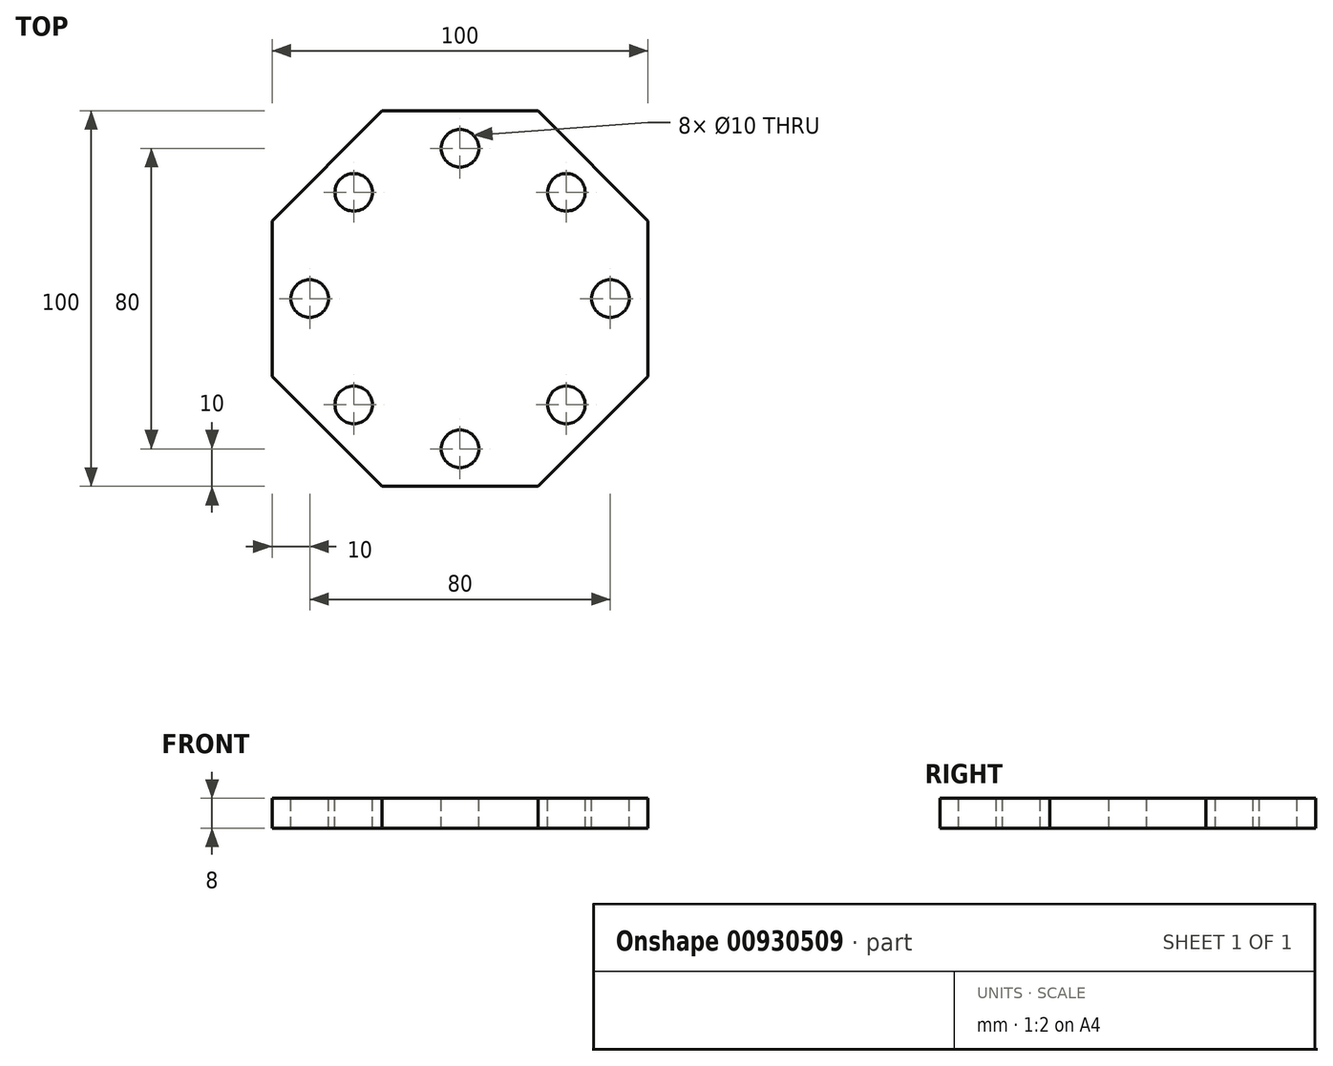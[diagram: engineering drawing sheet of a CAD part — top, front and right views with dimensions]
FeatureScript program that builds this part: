
annotation { "Feature Type Name" : "Feature", "Feature Type Description" : "" }
export const myFeature = defineFeature(function(context is Context, id is Id, definition is map)
    precondition{}
    {
        {
            var Q0;
            Q0=qCreatedBy(makeId("Top.planeOp"),FACE);
            var sketch = newSketch(context, id + "F0", { "sketchPlane" : qUnion([Q0])});
            skCircle(sketch, "E0.cCircle", {"center": v(0, 0) * mm, "radius": 50 * mm, "construction": true});
            skLineSegment(sketch, "E0.0", {"start": v(50, -20.71) * mm, "end": v(20.71, -50) * mm});
            skLineSegment(sketch, "E0.1", {"start": v(20.71, -50) * mm, "end": v(-20.71, -50) * mm});
            skLineSegment(sketch, "E0.2", {"start": v(-20.71, -50) * mm, "end": v(-50, -20.71) * mm});
            skLineSegment(sketch, "E0.3", {"start": v(-50, -20.71) * mm, "end": v(-50, 20.71) * mm});
            skLineSegment(sketch, "E0.4", {"start": v(-50, 20.71) * mm, "end": v(-20.71, 50) * mm});
            skLineSegment(sketch, "E0.5", {"start": v(-20.71, 50) * mm, "end": v(20.71, 50) * mm});
            skLineSegment(sketch, "E0.6", {"start": v(20.71, 50) * mm, "end": v(50, 20.71) * mm});
            skLineSegment(sketch, "E0.7", {"start": v(50, 20.71) * mm, "end": v(50, -20.71) * mm});
            skPoint(sketch, "E0.0.midPoint", {"position": v(35.36, -35.36) * mm});
            skSolve(sketch);
        }
        {
            var Q0;
            Q0 = qSketchRegion(id + "F0", true);
            extrude(context, id + "F1", {"entities" : qUnion([Q0]), "depth" : 8 * mm, "offsetDistance" : 25 * mm});
        }
        {
            var Q0;
            Q0=makeQuery(id+"F1.opExtrude","CAP_FACE",FACE,{"disambiguationData":[OSD([sQuery(id+"F0.wireOp",EDGE,"E0.0"),sQuery(id+"F0.wireOp",EDGE,"E0.1"),sQuery(id+"F0.wireOp",EDGE,"E0.2"),sQuery(id+"F0.wireOp",EDGE,"E0.3"),sQuery(id+"F0.wireOp",EDGE,"E0.4"),sQuery(id+"F0.wireOp",EDGE,"E0.5"),sQuery(id+"F0.wireOp",EDGE,"E0.6"),sQuery(id+"F0.wireOp",EDGE,"E0.7")])],"isStart":false});
            var sketch = newSketch(context, id + "F2", { "sketchPlane" : qUnion([Q0])});
            skCircle(sketch, "E1", {"center": v(0, 0) * mm, "radius": 40 * mm});
            skCircle(sketch, "E2", {"center": v(0, 40) * mm, "radius": 5 * mm});
            skCircle(sketch, "E3", {"center": v(0, -40) * mm, "radius": 5 * mm});
            skCircle(sketch, "E4", {"center": v(40, 0) * mm, "radius": 5 * mm});
            skCircle(sketch, "E5", {"center": v(-40, 0) * mm, "radius": 5 * mm});
            skCircle(sketch, "E6", {"center": v(-28.28, 28.28) * mm, "radius": 5 * mm});
            skCircle(sketch, "E7", {"center": v(28.28, 28.28) * mm, "radius": 5 * mm});
            skCircle(sketch, "E8", {"center": v(28.28, -28.28) * mm, "radius": 5 * mm});
            skCircle(sketch, "E9", {"center": v(-28.28, -28.28) * mm, "radius": 5 * mm});
            skSolve(sketch);
        }
        {
            var Q0;
            {var subQ0=sQuery(id+"F2.wireOp",EDGE,"E7");var subQ1=sQuery(id+"F2.wireOp",EDGE,"E1");var subQ2=makeQuery(id+"F2.imprint","INTERSECT",VERTEX,{"disambiguationData":[OD(0.0)],"derivedFrom":[subQ1,subQ0]});Q0=makeQuery(id+"F2.imprint","IMPRINT",FACE,{"disambiguationData":[TD([[makeQuery(id+"F2.imprint","IMPRINT",EDGE,{"disambiguationData":[TD([[subQ2,-1.0]])],"derivedFrom":subQ1}),1.0]])]});}
            var Q1;
            {var subQ0=sQuery(id+"F2.wireOp",EDGE,"E7");var subQ1=sQuery(id+"F2.wireOp",EDGE,"E1");var subQ2=makeQuery(id+"F2.imprint","INTERSECT",VERTEX,{"disambiguationData":[OD(0.0)],"derivedFrom":[subQ1,subQ0]});Q1=makeQuery(id+"F2.imprint","IMPRINT",FACE,{"disambiguationData":[TD([[makeQuery(id+"F2.imprint","IMPRINT",EDGE,{"disambiguationData":[TD([[subQ2,-1.0]])],"derivedFrom":subQ1}),-1.0]])]});}
            var Q2;
            {var subQ0=sQuery(id+"F2.wireOp",EDGE,"E2");var subQ1=sQuery(id+"F2.wireOp",EDGE,"E1");var subQ2=makeQuery(id+"F2.imprint","INTERSECT",VERTEX,{"disambiguationData":[OD(0.0)],"derivedFrom":[subQ1,subQ0]});Q2=makeQuery(id+"F2.imprint","IMPRINT",FACE,{"disambiguationData":[TD([[makeQuery(id+"F2.imprint","IMPRINT",EDGE,{"disambiguationData":[TD([[subQ2,-1.0]])],"derivedFrom":subQ1}),1.0]])]});}
            var Q3;
            {var subQ0=sQuery(id+"F2.wireOp",EDGE,"E2");var subQ1=sQuery(id+"F2.wireOp",EDGE,"E1");var subQ2=makeQuery(id+"F2.imprint","INTERSECT",VERTEX,{"disambiguationData":[OD(0.0)],"derivedFrom":[subQ1,subQ0]});Q3=makeQuery(id+"F2.imprint","IMPRINT",FACE,{"disambiguationData":[TD([[makeQuery(id+"F2.imprint","IMPRINT",EDGE,{"disambiguationData":[TD([[subQ2,-1.0]])],"derivedFrom":subQ1}),-1.0]])]});}
            var Q4;
            {var subQ0=sQuery(id+"F2.wireOp",EDGE,"E6");var subQ1=sQuery(id+"F2.wireOp",EDGE,"E1");var subQ2=makeQuery(id+"F2.imprint","INTERSECT",VERTEX,{"disambiguationData":[OD(0.0)],"derivedFrom":[subQ1,subQ0]});Q4=makeQuery(id+"F2.imprint","IMPRINT",FACE,{"disambiguationData":[TD([[makeQuery(id+"F2.imprint","IMPRINT",EDGE,{"disambiguationData":[TD([[subQ2,-1.0]])],"derivedFrom":subQ1}),-1.0]])]});}
            var Q5;
            {var subQ0=sQuery(id+"F2.wireOp",EDGE,"E6");var subQ1=sQuery(id+"F2.wireOp",EDGE,"E1");var subQ2=makeQuery(id+"F2.imprint","INTERSECT",VERTEX,{"disambiguationData":[OD(0.0)],"derivedFrom":[subQ1,subQ0]});Q5=makeQuery(id+"F2.imprint","IMPRINT",FACE,{"disambiguationData":[TD([[makeQuery(id+"F2.imprint","IMPRINT",EDGE,{"disambiguationData":[TD([[subQ2,-1.0]])],"derivedFrom":subQ1}),1.0]])]});}
            var Q6;
            {var subQ0=sQuery(id+"F2.wireOp",EDGE,"E5");var subQ1=sQuery(id+"F2.wireOp",EDGE,"E1");var subQ2=makeQuery(id+"F2.imprint","INTERSECT",VERTEX,{"disambiguationData":[OD(0.0)],"derivedFrom":[subQ1,subQ0]});Q6=makeQuery(id+"F2.imprint","IMPRINT",FACE,{"disambiguationData":[TD([[makeQuery(id+"F2.imprint","IMPRINT",EDGE,{"disambiguationData":[TD([[subQ2,-1.0]])],"derivedFrom":subQ1}),-1.0]])]});}
            var Q7;
            {var subQ0=sQuery(id+"F2.wireOp",EDGE,"E5");var subQ1=sQuery(id+"F2.wireOp",EDGE,"E1");var subQ2=makeQuery(id+"F2.imprint","INTERSECT",VERTEX,{"disambiguationData":[OD(0.0)],"derivedFrom":[subQ1,subQ0]});Q7=makeQuery(id+"F2.imprint","IMPRINT",FACE,{"disambiguationData":[TD([[makeQuery(id+"F2.imprint","IMPRINT",EDGE,{"disambiguationData":[TD([[subQ2,-1.0]])],"derivedFrom":subQ1}),1.0]])]});}
            var Q8;
            {var subQ0=sQuery(id+"F2.wireOp",EDGE,"E9");var subQ1=sQuery(id+"F2.wireOp",EDGE,"E1");var subQ2=makeQuery(id+"F2.imprint","INTERSECT",VERTEX,{"disambiguationData":[OD(0.0)],"derivedFrom":[subQ1,subQ0]});Q8=makeQuery(id+"F2.imprint","IMPRINT",FACE,{"disambiguationData":[TD([[makeQuery(id+"F2.imprint","IMPRINT",EDGE,{"disambiguationData":[TD([[subQ2,-1.0]])],"derivedFrom":subQ1}),-1.0]])]});}
            var Q9;
            {var subQ0=sQuery(id+"F2.wireOp",EDGE,"E9");var subQ1=sQuery(id+"F2.wireOp",EDGE,"E1");var subQ2=makeQuery(id+"F2.imprint","INTERSECT",VERTEX,{"disambiguationData":[OD(0.0)],"derivedFrom":[subQ1,subQ0]});Q9=makeQuery(id+"F2.imprint","IMPRINT",FACE,{"disambiguationData":[TD([[makeQuery(id+"F2.imprint","IMPRINT",EDGE,{"disambiguationData":[TD([[subQ2,-1.0]])],"derivedFrom":subQ1}),1.0]])]});}
            var Q10;
            {var subQ0=sQuery(id+"F2.wireOp",EDGE,"E3");var subQ1=sQuery(id+"F2.wireOp",EDGE,"E1");var subQ2=makeQuery(id+"F2.imprint","INTERSECT",VERTEX,{"disambiguationData":[OD(0.0)],"derivedFrom":[subQ1,subQ0]});Q10=makeQuery(id+"F2.imprint","IMPRINT",FACE,{"disambiguationData":[TD([[makeQuery(id+"F2.imprint","IMPRINT",EDGE,{"disambiguationData":[TD([[subQ2,-1.0]])],"derivedFrom":subQ1}),1.0]])]});}
            var Q11;
            {var subQ0=sQuery(id+"F2.wireOp",EDGE,"E3");var subQ1=sQuery(id+"F2.wireOp",EDGE,"E1");var subQ2=makeQuery(id+"F2.imprint","INTERSECT",VERTEX,{"disambiguationData":[OD(0.0)],"derivedFrom":[subQ1,subQ0]});Q11=makeQuery(id+"F2.imprint","IMPRINT",FACE,{"disambiguationData":[TD([[makeQuery(id+"F2.imprint","IMPRINT",EDGE,{"disambiguationData":[TD([[subQ2,-1.0]])],"derivedFrom":subQ1}),-1.0]])]});}
            var Q12;
            {var subQ0=sQuery(id+"F2.wireOp",EDGE,"E8");var subQ1=sQuery(id+"F2.wireOp",EDGE,"E1");var subQ2=makeQuery(id+"F2.imprint","INTERSECT",VERTEX,{"disambiguationData":[OD(0.0)],"derivedFrom":[subQ1,subQ0]});Q12=makeQuery(id+"F2.imprint","IMPRINT",FACE,{"disambiguationData":[TD([[makeQuery(id+"F2.imprint","IMPRINT",EDGE,{"disambiguationData":[TD([[subQ2,-1.0]])],"derivedFrom":subQ1}),1.0]])]});}
            var Q13;
            {var subQ0=sQuery(id+"F2.wireOp",EDGE,"E8");var subQ1=sQuery(id+"F2.wireOp",EDGE,"E1");var subQ2=makeQuery(id+"F2.imprint","INTERSECT",VERTEX,{"disambiguationData":[OD(0.0)],"derivedFrom":[subQ1,subQ0]});Q13=makeQuery(id+"F2.imprint","IMPRINT",FACE,{"disambiguationData":[TD([[makeQuery(id+"F2.imprint","IMPRINT",EDGE,{"disambiguationData":[TD([[subQ2,-1.0]])],"derivedFrom":subQ1}),-1.0]])]});}
            var Q14;
            {var subQ0=sQuery(id+"F2.wireOp",EDGE,"E4");var subQ1=sQuery(id+"F2.wireOp",EDGE,"E1");var subQ2=makeQuery(id+"F2.imprint","INTERSECT",VERTEX,{"disambiguationData":[OD(0.0)],"derivedFrom":[subQ1,subQ0]});Q14=makeQuery(id+"F2.imprint","IMPRINT",FACE,{"disambiguationData":[TD([[makeQuery(id+"F2.imprint","IMPRINT",EDGE,{"disambiguationData":[TD([[subQ2,1.0]])],"derivedFrom":subQ1}),1.0]])]});}
            var Q15;
            {var subQ0=sQuery(id+"F2.wireOp",EDGE,"E4");var subQ1=sQuery(id+"F2.wireOp",EDGE,"E1");var subQ2=makeQuery(id+"F2.imprint","INTERSECT",VERTEX,{"disambiguationData":[OD(0.0)],"derivedFrom":[subQ1,subQ0]});Q15=makeQuery(id+"F2.imprint","IMPRINT",FACE,{"disambiguationData":[TD([[makeQuery(id+"F2.imprint","IMPRINT",EDGE,{"disambiguationData":[TD([[subQ2,1.0]])],"derivedFrom":subQ1}),-1.0]])]});}
            extrude(context, id + "F3", {"entities" : qUnion([Q0, Q1, Q2, Q3, Q4, Q5, Q6, Q7, Q8, Q9, Q10, Q11, Q12, Q13, Q14, Q15]), "operationType" : NewBodyOperationType.REMOVE, "oppositeDirection" : true, "depth" : 25 * mm, "offsetDistance" : 25 * mm});
        }
    });
